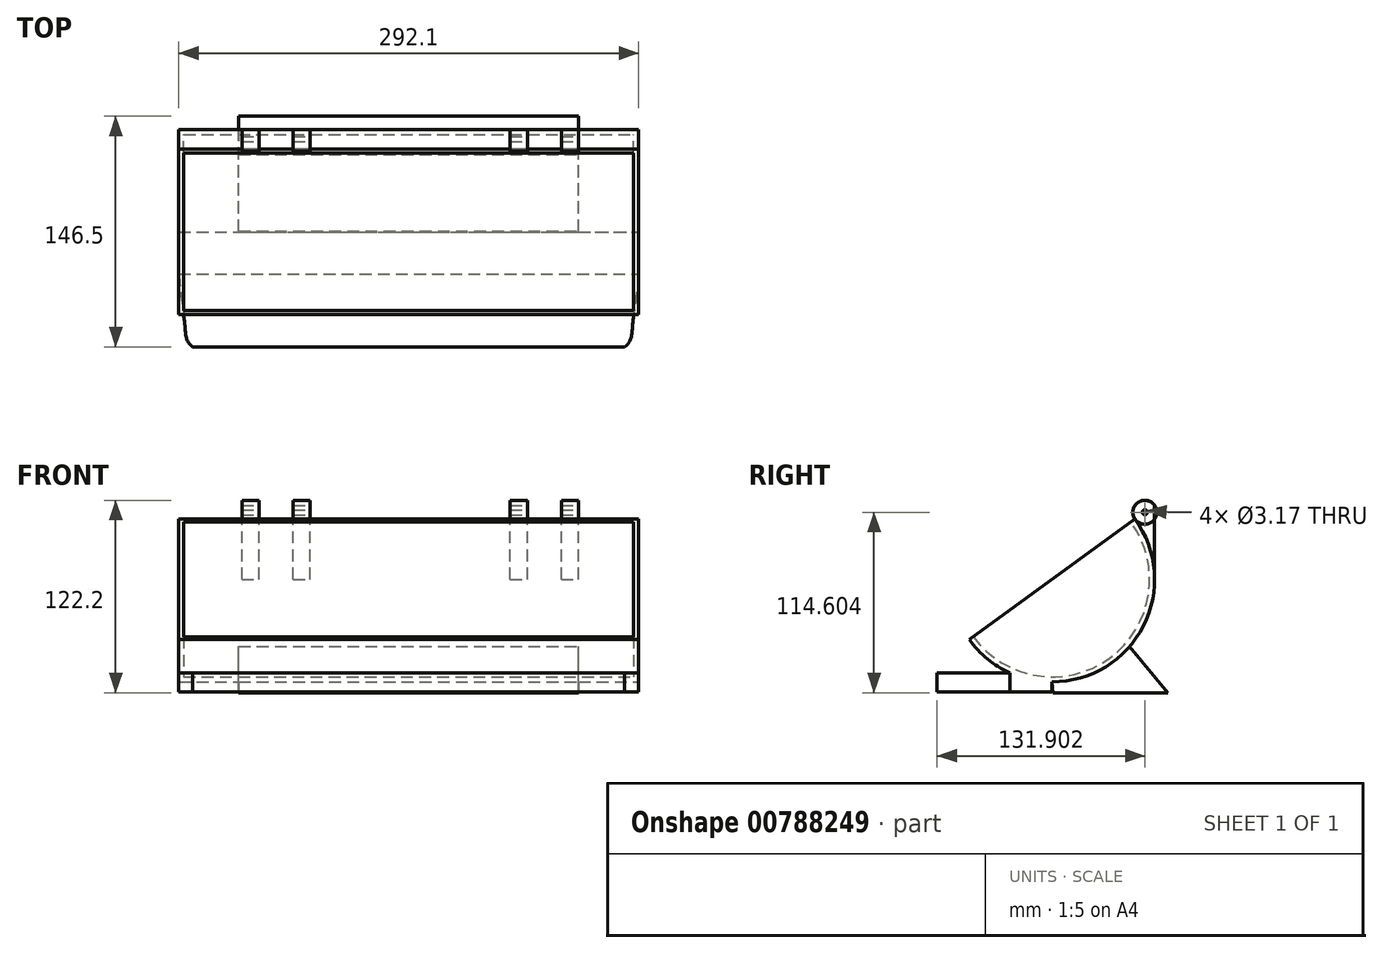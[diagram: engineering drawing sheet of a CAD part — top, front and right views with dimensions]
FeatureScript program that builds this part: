
annotation { "Feature Type Name" : "Feature", "Feature Type Description" : "" }
export const myFeature = defineFeature(function(context is Context, id is Id, definition is map)
    precondition{}
    {
        {
            var Q0;
            Q0=qCreatedBy(makeId("Right.planeOp"),FACE);
            var sketch = newSketch(context, id + "F0", { "sketchPlane" : qUnion([Q0])});
            skCircle(sketch, "E0", {"center": v(0, 0) * mm, "radius": 65.09 * mm});
            skLineSegment(sketch, "E1", {"start": v(-52.66, -38.26) * mm, "end": v(52.66, 38.26) * mm});
            skSolve(sketch);
        }
        {
            var Q0;
            {var subQ0=sQuery(id+"F0.wireOp",EDGE,"E1");Q0=makeQuery(id+"F0.imprint","IMPRINT",FACE,{"disambiguationData":[TD([[makeQuery(id+"F0.imprint","IMPRINT",EDGE,{"derivedFrom":subQ0}),-1.0]])]});}
            extrude(context, id + "F1", {"entities" : qUnion([Q0]), "depth" : 292.1 * mm, "offsetDistance" : 25.4 * mm});
        }
        {
            var Q0;
            Q0=makeQuery(id+"F1.opExtrude","SWEPT_FACE",FACE,{"disambiguationData":[OSD([sQuery(id+"F0.wireOp",EDGE,"E1")])]});
            var sketch = newSketch(context, id + "F2", { "sketchPlane" : qUnion([Q0])});
            skLineSegment(sketch, "E2.0", {"start": v(288.93, 61.91) * mm, "end": v(3.17, 61.91) * mm});
            skLineSegment(sketch, "E2.1", {"start": v(288.93, -61.91) * mm, "end": v(288.93, 61.91) * mm});
            skLineSegment(sketch, "E2.2", {"start": v(288.93, -61.91) * mm, "end": v(3.17, -61.91) * mm});
            skLineSegment(sketch, "E2.3", {"start": v(3.17, -61.91) * mm, "end": v(3.17, 61.91) * mm});
            skLineSegment(sketch, "E3", {"start": v(3.17, 0) * mm, "end": v(288.93, 0) * mm});
            skSolve(sketch);
        }
        {
            var Q0;
            {var subQ0=sQuery(id+"F2.wireOp",EDGE,"E2.2");Q0=makeQuery(id+"F2.imprint","IMPRINT",FACE,{"disambiguationData":[TD([[makeQuery(id+"F2.imprint","IMPRINT",EDGE,{"derivedFrom":subQ0}),-1.0]])]});}
            var Q1;
            Q1=sQuery(id+"F2.wireOp",EDGE,"E3");
            revolve(context, id + "F3", {"operationType" : NewBodyOperationType.REMOVE, "surfaceOperationType" : NewSurfaceOperationType.NEW, "entities" : qUnion([Q0]), "axis" : qUnion([Q1]), "revolveType" : RevolveType.FULL, "oppositeDirection" : true});
        }
        {
            var Q0;
            Q0=makeQuery(id+"F1.opExtrude","CAP_FACE",FACE,{"disambiguationData":[OSD([sQuery(id+"F0.wireOp",EDGE,"E0"),sQuery(id+"F0.wireOp",EDGE,"E1")])],"isStart":false});
            var sketch = newSketch(context, id + "F4", { "sketchPlane" : qUnion([Q0])});
            skLineSegment(sketch, "E4", {"start": v(0.45, -71.98) * mm, "end": v(73.47, -71.98) * mm});
            skLineSegment(sketch, "E5", {"start": v(0, -65.09) * mm, "end": v(0.45, -71.98) * mm});
            skLineSegment(sketch, "E6", {"start": v(73.47, -71.98) * mm, "end": v(49.2, -42.61) * mm});
            skSolve(sketch);
        }
        {
            var Q0;
            {var subQ0=sQuery(id+"F4.wireOp",EDGE,"E4");Q0=makeQuery(id+"F4.imprint","IMPRINT",FACE,{"disambiguationData":[TD([[makeQuery(id+"F4.imprint","IMPRINT",EDGE,{"derivedFrom":subQ0}),1.0]])]});}
            extrude(context, id + "F5", {"entities" : qUnion([Q0]), "oppositeDirection" : true, "depth" : 215.9 * mm, "offsetDistance" : 25.4 * mm});
        }
        {
            var Q0;
            Q0=makeQuery(id+"F5.opExtrude","SWEPT_BODY",BODY,{"disambiguationData":[OSD([sQuery(id+"F0.wireOp",EDGE,"E0"),sQuery(id+"F4.wireOp",EDGE,"E4"),sQuery(id+"F4.wireOp",EDGE,"KYubqp39-4rkq-0Sul-4jHG-rVcmojZrJ8TJ")])]});
            transform(context, id + "F6", {"entities" : qUnion([Q0]), "transformType" : TransformType.TRANSLATION_3D, "dx" : -38.1 * mm, "dy" : 0 * mm, "dz" : 0 * mm, "makeCopy" : false});
        }
        {
            var Q0;
            Q0=makeQuery(id+"F1.opExtrude","CAP_FACE",FACE,{"disambiguationData":[OSD([sQuery(id+"F0.wireOp",EDGE,"E0"),sQuery(id+"F0.wireOp",EDGE,"E1")])],"isStart":false});
            var sketch = newSketch(context, id + "F7", { "sketchPlane" : qUnion([Q0])});
            skLineSegment(sketch, "E7", {"start": v(0, -71.44) * mm, "end": v(-73.03, -71.44) * mm});
            skLineSegment(sketch, "E8", {"start": v(-73.03, -71.44) * mm, "end": v(-73.03, -59.3) * mm});
            skLineSegment(sketch, "E9", {"start": v(-73.03, -59.3) * mm, "end": v(-26.84, -59.3) * mm});
            skLineSegment(sketch, "E10", {"start": v(0, -71.44) * mm, "end": v(0, -65.09) * mm});
            skPoint(sketch, "E11.0", {"position": v(0, 0) * mm});
            skArc(sketch, "E12", {"start": v(0, -65.09) * mm, "mid": v(-13.73, -63.62) * mm, "end": v(-26.84, -59.3) * mm});
            skSolve(sketch);
        }
        {
            var Q0;
            Q0=makeQuery(id+"F7.imprint","IMPRINT",FACE,{"disambiguationData":[TD([[makeQuery(id+"F7.imprint","IMPRINT",EDGE,{"derivedFrom":sQuery(id+"F7.wireOp",EDGE,"E7")}),-1.0]])]});
            extrude(context, id + "F8", {"entities" : qUnion([Q0]), "operationType" : NewBodyOperationType.ADD, "oppositeDirection" : true, "depth" : 292.1 * mm, "offsetDistance" : 25.4 * mm});
        }
        {
            var Q0;
            Q0=makeQuery(id+"F8.opExtrude","SWEPT_FACE",FACE,{"disambiguationData":[OSD([sQuery(id+"F7.wireOp",EDGE,"E9")])]});
            var sketch = newSketch(context, id + "F9", { "sketchPlane" : qUnion([Q0])});
            skLineSegment(sketch, "E13", {"start": v(0, -73.03) * mm, "end": v(8.9, -73.03) * mm});
            skLineSegment(sketch, "E14", {"start": v(0, -26.84) * mm, "end": v(0, -73.03) * mm});
            skFitSpline(sketch, "E15", {"points": [v(0, -26.84) * mm, v(1.7, -42.08) * mm, v(3.9, -59.84) * mm, v(8.9, -73.03) * mm], "startDerivative": vector(5.58, -44.82) * mm, "endDerivative": vector(42.2, -26.09) * mm});
            skLineSegment(sketch, "E16", {"start": v(146.05, -73.03) * mm, "end": v(146.05, -36.08) * mm});
            skFitSpline(sketch, "E17.MirrorCS", {"points": [v(292.1, -26.84) * mm, v(290.4, -42.08) * mm, v(288.2, -59.84) * mm, v(283.21, -73.02) * mm], "startDerivative": vector(-5.58, -44.82) * mm, "endDerivative": vector(-42.2, -26.09) * mm});
            skSolve(sketch);
        }
        {
            var Q0;
            Q0=makeQuery(id+"F9.imprint","IMPRINT",FACE,{"disambiguationData":[TD([[makeQuery(id+"F9.imprint","IMPRINT",EDGE,{"derivedFrom":sQuery(id+"F9.wireOp",EDGE,"E13")}),1.0]])]});
            extrude(context, id + "F10", {"entities" : qUnion([Q0]), "operationType" : NewBodyOperationType.REMOVE, "oppositeDirection" : true, "depth" : 25.4 * mm, "offsetDistance" : 25.4 * mm});
        }
        {
            var Q0;
            {var subQ0=sQuery(id+"F9.wireOp",EDGE,"E17.MirrorCS");Q0=makeQuery(id+"F9.imprint","IMPRINT",FACE,{"disambiguationData":[TD([[makeQuery(id+"F9.imprint","IMPRINT",EDGE,{"derivedFrom":subQ0}),1.0]])]});}
            extrude(context, id + "F11", {"entities" : qUnion([Q0]), "operationType" : NewBodyOperationType.REMOVE, "oppositeDirection" : true, "depth" : 25.4 * mm, "offsetDistance" : 25.4 * mm});
        }
        {
            var Q0;
            Q0=makeQuery(id+"F8.boolean.opBoolean","MERGE",FACE,{"derivedFrom":[makeQuery(id+"F1.opExtrude","CAP_FACE",FACE,{"disambiguationData":[OSD([sQuery(id+"F0.wireOp",EDGE,"E0"),sQuery(id+"F0.wireOp",EDGE,"E1")])],"isStart":false}),makeQuery(id+"F8.opExtrude","CAP_FACE",FACE,{"disambiguationData":[OSD([sQuery(id+"F7.wireOp",EDGE,"E7"),sQuery(id+"F7.wireOp",EDGE,"E8"),sQuery(id+"F7.wireOp",EDGE,"E9"),sQuery(id+"F7.wireOp",EDGE,"E10"),sQuery(id+"F7.wireOp",EDGE,"E12")])],"isStart":true})]});
            var sketch = newSketch(context, id + "F12", { "sketchPlane" : qUnion([Q0])});
            skLineSegment(sketch, "E18", {"start": v(65.09, 0) * mm, "end": v(65.09, 47) * mm});
            skPoint(sketch, "E19.0", {"position": v(52.66, 38.26) * mm});
            skArc(sketch, "E20", {"start": v(52.66, 38.26) * mm, "mid": v(61.9, 20.11) * mm, "end": v(65.09, 0) * mm});
            skLineSegment(sketch, "E21", {"start": v(52.66, 38.26) * mm, "end": v(65.09, 47) * mm, "construction": true});
            skArc(sketch, "E22", {"start": v(65.09, 47) * mm, "mid": v(54.42, 48.78) * mm, "end": v(52.78, 38.08) * mm});
            skCircle(sketch, "E23", {"center": v(58.87, 42.62) * mm, "radius": 1.59 * mm});
            skSolve(sketch);
        }
        {
            var Q0;
            Q0 = qSketchRegion(id + "F12", true);
            extrude(context, id + "F13", {"entities" : qUnion([Q0]), "oppositeDirection" : true, "depth" : 10.92 * mm, "offsetDistance" : 25.4 * mm});
        }
        {
            var Q0;
            Q0=makeQuery(id+"F13.opExtrude","SWEPT_BODY",BODY,{"disambiguationData":[OSD([sQuery(id+"F12.wireOp",EDGE,"E18"),sQuery(id+"F12.wireOp",EDGE,"E20"),sQuery(id+"F12.wireOp",EDGE,"E22"),sQuery(id+"F12.wireOp",EDGE,"E23")])]});
            transform(context, id + "F14", {"entities" : qUnion([Q0]), "transformType" : TransformType.TRANSLATION_3D, "dx" : -38.1 * mm, "dy" : 0 * mm, "dz" : 0 * mm, "makeCopy" : false});
        }
        {
            var Q0;
            Q0=makeQuery(id+"F13.opExtrude","SWEPT_BODY",BODY,{"disambiguationData":[OSD([sQuery(id+"F12.wireOp",EDGE,"E18"),sQuery(id+"F12.wireOp",EDGE,"E20"),sQuery(id+"F12.wireOp",EDGE,"E22"),sQuery(id+"F12.wireOp",EDGE,"E23")])]});
            transform(context, id + "F15", {"entities" : qUnion([Q0]), "transformType" : TransformType.TRANSLATION_3D, "dx" : -32.5 * mm, "dy" : 0 * mm, "dz" : 0 * mm, "makeCopy" : true});
        }
        {
            var Q0;
            Q0=makeQuery(id+"F15.opPattern","COPY",BODY,{"derivedFrom":makeQuery(id+"F13.opExtrude","SWEPT_BODY",BODY,{"disambiguationData":[OSD([sQuery(id+"F12.wireOp",EDGE,"E18"),sQuery(id+"F12.wireOp",EDGE,"E20"),sQuery(id+"F12.wireOp",EDGE,"E22"),sQuery(id+"F12.wireOp",EDGE,"E23")])]}),"instanceName":"1"});
            var Q1;
            {var subQ0=sQuery(id+"F0.wireOp",EDGE,"E1");var subQ1=sQuery(id+"F0.wireOp",EDGE,"E0");Q1=makeQuery(id+"F1.opExtrude","SWEPT_EDGE",EDGE,{"disambiguationData":[OSD([subQ1,subQ0]),TDD([makeQuery(id+"F0.imprint","INTERSECT",VERTEX,{"disambiguationData":[OD(1.0)],"derivedFrom":[subQ1,subQ0]})])]});}
            transform(context, id + "F16", {"entities" : qUnion([Q0]), "transformType" : TransformType.TRANSLATION_DISTANCE, "transformDirection" : qUnion([Q1]), "distance" : 137.92 * mm, "makeCopy" : true});
        }
        {
            var Q0;
            Q0=makeQuery(id+"F16.opPattern","COPY",BODY,{"derivedFrom":makeQuery(id+"F15.opPattern","COPY",BODY,{"derivedFrom":makeQuery(id+"F13.opExtrude","SWEPT_BODY",BODY,{"disambiguationData":[OSD([sQuery(id+"F12.wireOp",EDGE,"E18"),sQuery(id+"F12.wireOp",EDGE,"E20"),sQuery(id+"F12.wireOp",EDGE,"E22"),sQuery(id+"F12.wireOp",EDGE,"E23")])]}),"instanceName":"1"}),"instanceName":"1"});
            transform(context, id + "F17", {"entities" : qUnion([Q0]), "transformType" : TransformType.TRANSLATION_3D, "dx" : -32.5 * mm, "dy" : 0 * mm, "dz" : 0 * mm, "makeCopy" : true});
        }
    });
